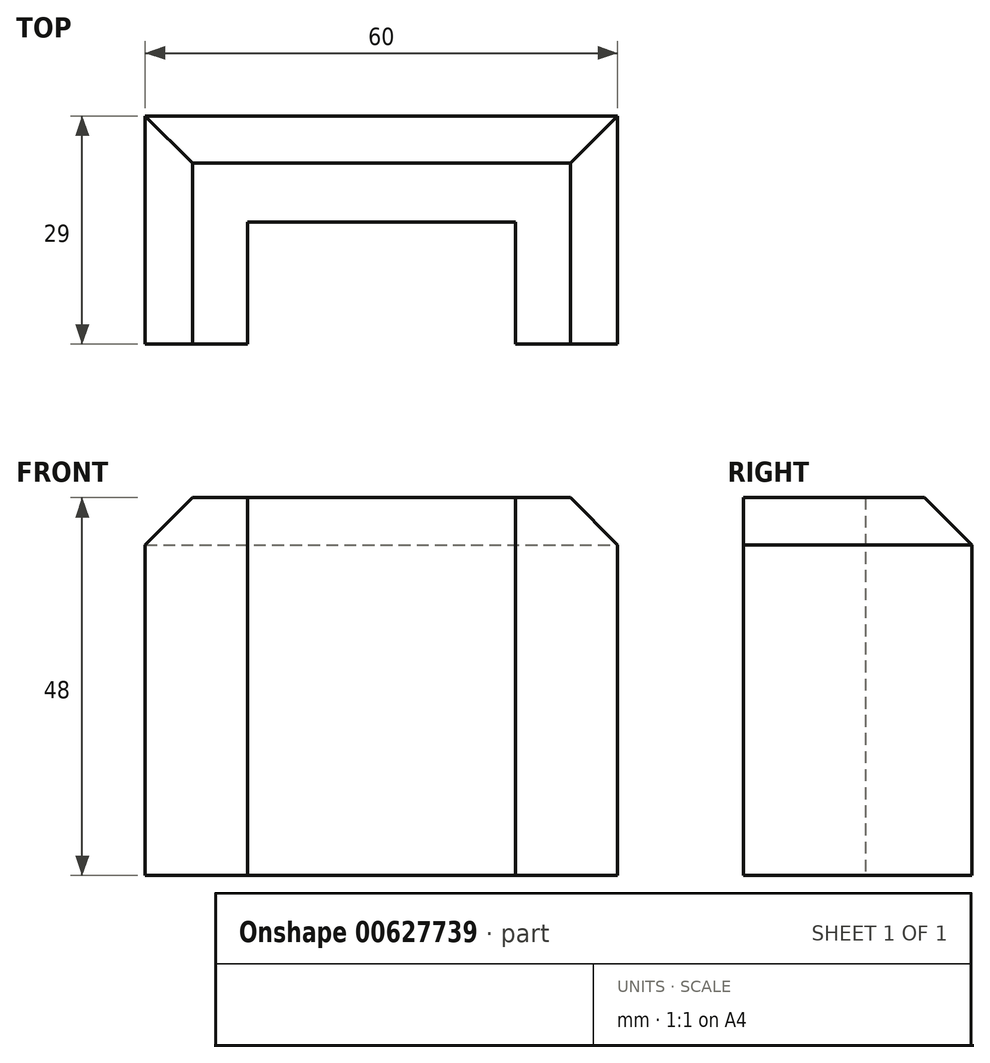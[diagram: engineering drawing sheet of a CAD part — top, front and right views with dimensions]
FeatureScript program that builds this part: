
annotation { "Feature Type Name" : "Feature", "Feature Type Description" : "" }
export const myFeature = defineFeature(function(context is Context, id is Id, definition is map)
    precondition{}
    {
        {
            var Q0;
            Q0=qCreatedBy(makeId("Top.planeOp"),FACE);
            var sketch = newSketch(context, id + "F0", { "sketchPlane" : qUnion([Q0])});
            skLineSegment(sketch, "E0.top", {"start": v(0, 29) * mm, "end": v(-30, 29) * mm});
            skLineSegment(sketch, "E0.right", {"start": v(-30, 0) * mm, "end": v(-30, 29) * mm});
            skPoint(sketch, "E1.oppositeSnap0", {"position": v(-17, 0) * mm});
            skLineSegment(sketch, "E1.top", {"start": v(0, 15.5) * mm, "end": v(-17, 15.5) * mm});
            skLineSegment(sketch, "E2.MirrorCS", {"start": v(0, 15.5) * mm, "end": v(17, 15.5) * mm});
            skLineSegment(sketch, "E3.MirrorCS", {"start": v(0, 29) * mm, "end": v(30, 29) * mm});
            skLineSegment(sketch, "E4.MirrorCS", {"start": v(30, 0) * mm, "end": v(30, 29) * mm});
            skLineSegment(sketch, "E5", {"start": v(-30, 0) * mm, "end": v(-17, 0) * mm});
            skLineSegment(sketch, "E6.MirrorCS", {"start": v(30, 0) * mm, "end": v(17, 0) * mm});
            skLineSegment(sketch, "E7", {"start": v(-17, 0) * mm, "end": v(-17, 15.5) * mm});
            skLineSegment(sketch, "E8.MirrorCS", {"start": v(17, 0) * mm, "end": v(17, 15.5) * mm});
            skSolve(sketch);
        }
        {
            var Q0;
            Q0 = qSketchRegion(id + "F0", true);
            extrude(context, id + "F1", {"entities" : qUnion([Q0]), "depth" : 48 * mm, "offsetDistance" : 25 * mm});
        }
        {
            var Q0;
            Q0=makeQuery(id+"F1.opExtrude","CAP_EDGE",EDGE,{"disambiguationData":[OSD([sQuery(id+"F0.wireOp",EDGE,"E0.top"),sQuery(id+"F0.wireOp",EDGE,"E3.MirrorCS")])],"isStart":false});
            var Q1;
            Q1=makeQuery(id+"F1.opExtrude","CAP_EDGE",EDGE,{"disambiguationData":[OSD([sQuery(id+"F0.wireOp",EDGE,"E0.right")])],"isStart":false});
            var Q2;
            Q2=makeQuery(id+"F1.opExtrude","CAP_EDGE",EDGE,{"disambiguationData":[OSD([sQuery(id+"F0.wireOp",EDGE,"E4.MirrorCS")])],"isStart":false});
            chamfer(context, id + "F2", {"entities" : qUnion([Q0, Q1, Q2]), "width" : 6 * mm, "tangentPropagation" : true});
        }
    });
